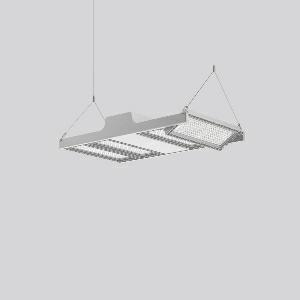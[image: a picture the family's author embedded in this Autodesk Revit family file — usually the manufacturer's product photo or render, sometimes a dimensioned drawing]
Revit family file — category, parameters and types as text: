
# Revit family: light_case_921688_004_1_76_f381
name_source: partatom
category: Lighting Fixtures
units: mm (PartAtom-declared; Revit-internal decimal feet)

## family parameters
Cut with Voids When Loaded = No
Host = Face
Light Source = No
Part Type = Normal
Room Calculation Point = No
Round Connector Dimension = Use Diameter
Shared = No

## types (1)
- LIGHT CASE (1 x LED Modul 865, 8700 lm, 6500)
    Apparent Load = 225 VA
    CIE Flux Codes = 80 98 100 100 100
    Color Rendering = 80
    Color Temperature = 6500
    Default Elevation = 1800 mm
    Description = Series: LIGHT CASE
Flat highbay luminaire for chain or cable suspension with 4 LED modules that can be swivelled. Housing: die cast aluminium and sheet steel, powder-coated. Optimised thermal management thanks to special luminaire design. Self-cleaning heat sink for constant heat dissipation. Cover: plastic (polycarbonate, shockproof), with integrated four-row lens system. LED modules can be swivelled ± 30° for optimum illumination. Suitable for chain or steel cable suspension (to be provided on site). With 5-pin connection terminal (1.5 m). With integrated movement sensor and light sensor for daylight detection on request. Ball impact proof in accordance with DIN 18032-03 (except steel cable suspension). Luminaire with limited surface temperature in accordance with EN 60598-2-24 for use in environments in which a deposit of conductive dust on the luminaire can be expected. 
Colour: silver, matt (approx. RAL 9006)
Length: 680 mm
Width: 397 mm
Height: 110 mm
Lamp: LED
Socket: without socket
Colour temperature: 6500K
Colour rendering index (CRI): 80
System power: 225 W
Rated luminous flux: 34800 lm
Luminous efficiency: 155 lm/W
Control gear: Converter, dimmable, DALI
Protection class: I
Type of protection: IP 65
    Height = 110 mm
    Lamp = 1 x LED Modul 865
    Lamp Light Flux = 8700 lm
    Lamp count = 1
    Length = 680 mm
    Lifetime = 50000 h
    Luminous efficacy = 155 lm/W
    Manufacturer = RZB
    ModVariant = No
    Model = 921688.004.1.76
    Mounting Place = Ceiling
    Mounting Type = Pendant
    Number of Poles = 1
    OnlyDefault = Yes
    Power Factor = 1
    Product Name = LIGHT CASE
    Product group = Pendant commercial luminaires
    ProductGroupID = 903
    Protection Class = Protection class I
    Protection Degree = IP 65
    RLX_Detail_Level = 1
    RLX_Emergency_Light_Flux = 0 lm
    RLX_Emergency_Type = 0
    RLX_Emergency_Type_DB = No
    RlxData = <blob elided: 27853 chars, md5=e12d5e8e>
    Socket = socket
    Standby Power = 0 W
    System Light Flux = 34800 lm
    System Power = 225 W
    Type Comments = Product without accessories
    Type Image = 921523.004.76.jpg
    URL = http://relux.com
    VarID = ---
    Voltage = 230 V
    Voltage Range = 220-240 V
    Weight = 0.00 kg
    Width = 397 mm

## geometry (parser evidence)
native form markers: Blend x4, Sweep x21
no freeform markers — native parametric forms only
